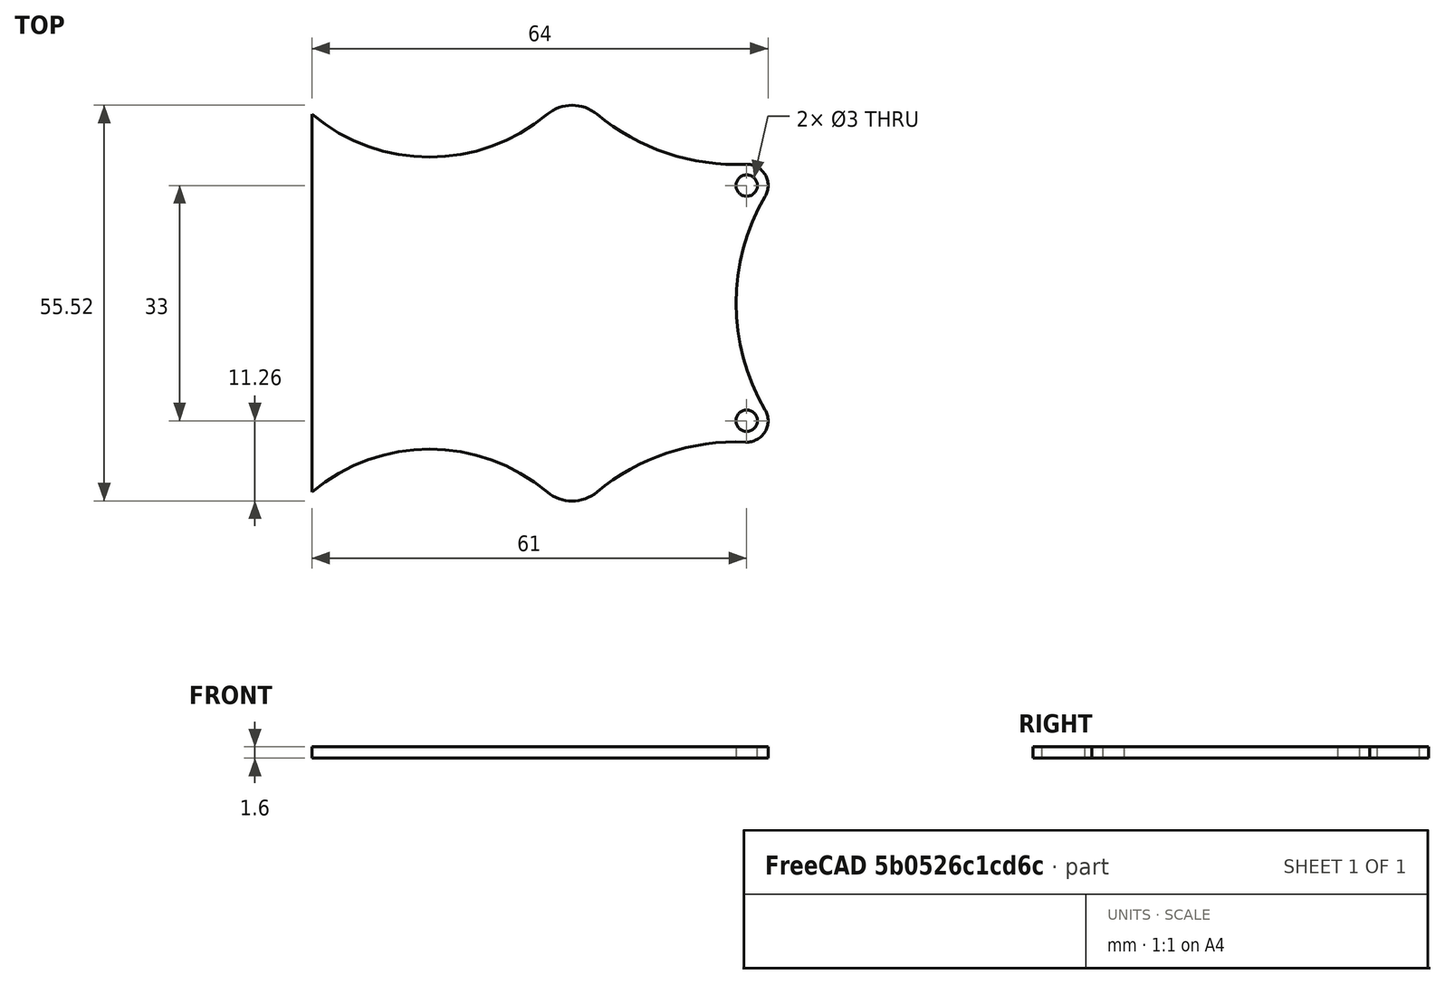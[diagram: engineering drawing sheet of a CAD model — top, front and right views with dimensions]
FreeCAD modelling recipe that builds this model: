
FCSTD DOCUMENT  (FreeCAD 0.19R24366 (Git))
Label: nixiePanelShape
License: All rights reserved
LicenseURL: http://en.wikipedia.org/wiki/All_rights_reserved
objects: Sketcher::SketchObject×1, PartDesign::Pad×1, PartDesign::Body×1
note: 4 computed .brp shape members not serialized (recipe doc carries the construction recipe); baked Part::Feature solids carry a one-line shape summary decoded from their .brp

FEATURE [Sketcher::SketchObject] Sketch
  FullyConstrained = false
  MapMode = 5
  Support = -> [XY_Plane]
  sketch-geometry (63):
    g0: LineSegment StartX=-6.5438e-12 StartY=-1.64544e-11 StartZ=0 EndX=86 EndY=-1.64544e-11 EndZ=0
    g1: LineSegment StartX=86 StartY=-1.64544e-11 StartZ=0 EndX=86 EndY=53 EndZ=0
    g2: LineSegment StartX=86 StartY=53 StartZ=0 EndX=-6.537e-12 EndY=53 EndZ=0
    g3: LineSegment StartX=-6.5438e-12 StartY=53 StartZ=0 EndX=-6.5438e-12 EndY=-1.64562e-11 EndZ=0
    g4: LineSegment StartX=3 StartY=44.5 StartZ=0 EndX=83 EndY=44.5 EndZ=0
    g5: LineSegment StartX=83 StartY=44.5 StartZ=0 EndX=83 EndY=8.5 EndZ=0
    g6: LineSegment StartX=83 StartY=8.5 StartZ=0 EndX=3 EndY=8.5 EndZ=0
    g7: LineSegment StartX=3 StartY=8.5 StartZ=0 EndX=3 EndY=44.5 EndZ=0
    g8: LineSegment StartX=3 StartY=8.5 StartZ=0 EndX=5.8074e-12 EndY=1.64544e-11 EndZ=0
    g9: LineSegment StartX=83 StartY=8.5 StartZ=0 EndX=86 EndY=-1.64544e-11 EndZ=0
    g10: LineSegment StartX=83 StartY=44.5 StartZ=0 EndX=86 EndY=53 EndZ=0
    g11: LineSegment StartX=-6.5438e-12 StartY=53 StartZ=0 EndX=3 EndY=44.5 EndZ=0
    g12: LineSegment StartX=-7 StartY=-23.5 StartZ=0 EndX=93 EndY=-23.5 EndZ=0
    g13: LineSegment StartX=93 StartY=-23.5 StartZ=0 EndX=93 EndY=76.5 EndZ=0
    g14: LineSegment StartX=93 StartY=76.5 StartZ=0 EndX=-7 EndY=76.5 EndZ=0
    g15: LineSegment StartX=-7 StartY=76.5 StartZ=0 EndX=-7 EndY=-23.5 EndZ=0
    g16: LineSegment StartX=0 StartY=0 StartZ=0 EndX=-7 EndY=-23.5 EndZ=0
    g17: LineSegment StartX=86 StartY=-1.64544e-11 StartZ=0 EndX=93 EndY=-23.5 EndZ=0
    g18: LineSegment StartX=-7 StartY=76.5 StartZ=0 EndX=-6.5441e-12 EndY=53 EndZ=0
    g19: LineSegment StartX=93 StartY=76.5 StartZ=0 EndX=86 EndY=53 EndZ=0
    g20: Circle CenterX=87.5 CenterY=43 CenterZ=0 NormalX=0 NormalY=0 NormalZ=1 AngleXU=0 Radius=1.5
    g21: Circle CenterX=87.5 CenterY=10 CenterZ=0 NormalX=0 NormalY=0 NormalZ=1 AngleXU=0 Radius=1.5
    g22: Circle CenterX=-1.5 CenterY=10 CenterZ=0 NormalX=0 NormalY=0 NormalZ=1 AngleXU=0 Radius=1.5
    g23: Circle CenterX=-1.5 CenterY=43 CenterZ=0 NormalX=0 NormalY=0 NormalZ=1 AngleXU=0 Radius=1.5
    g24: Circle CenterX=-1.5 CenterY=43 CenterZ=0 NormalX=0 NormalY=0 NormalZ=1 AngleXU=0 Radius=3
    g25: Circle CenterX=-1.5 CenterY=10 CenterZ=0 NormalX=0 NormalY=0 NormalZ=1 AngleXU=0 Radius=3
    g26: Circle CenterX=87.5 CenterY=10 CenterZ=0 NormalX=0 NormalY=0 NormalZ=1 AngleXU=0 Radius=3
    g27: Circle CenterX=87.5 CenterY=43 CenterZ=0 NormalX=0 NormalY=0 NormalZ=1 AngleXU=0 Radius=3
    g28: Circle CenterX=115.5 CenterY=26.5 CenterZ=0 NormalX=0 NormalY=0 NormalZ=1 AngleXU=0 Radius=29.5
    g29: Circle CenterX=-29.5 CenterY=26.5 CenterZ=0 NormalX=0 NormalY=0 NormalZ=1 AngleXU=0 Radius=29.5
    g30: LineSegment StartX=-1.36453e-11 StartY=63 StartZ=0 EndX=19.5 EndY=63 EndZ=0
    g31: LineSegment StartX=19.5 StartY=63 StartZ=0 EndX=26.5 EndY=63 EndZ=0
    g32: LineSegment StartX=26.5 StartY=63 StartZ=0 EndX=59.5 EndY=63 EndZ=0
    g33: LineSegment StartX=59.5 StartY=63 StartZ=0 EndX=66.5 EndY=63 EndZ=0
    g34: LineSegment StartX=66.5 StartY=63 StartZ=0 EndX=86 EndY=63 EndZ=0
    g35: LineSegment StartX=19.5 StartY=76.5 StartZ=0 EndX=19.5 EndY=-23.5 EndZ=0
    g36: LineSegment StartX=26.5 StartY=76.5 StartZ=0 EndX=26.5 EndY=-23.5 EndZ=0
    g37: LineSegment StartX=59.5 StartY=76.5 StartZ=0 EndX=59.5 EndY=-23.5 EndZ=0
    g38: LineSegment StartX=66.5 StartY=76.5 StartZ=0 EndX=66.5 EndY=-23.5 EndZ=0
    g39: Circle CenterX=1.43817e-11 CenterY=-23.5144 CenterZ=0 NormalX=0 NormalY=0 NormalZ=1 AngleXU=0 Radius=30.5479
    g40: LineSegment StartX=3 StartY=8.5 StartZ=0 EndX=19.5 EndY=-1.8062e-11 EndZ=0
    g41: Circle CenterX=86 CenterY=-23.5144 CenterZ=0 NormalX=0 NormalY=0 NormalZ=1 AngleXU=0 Radius=30.5479
    g42: Circle CenterX=0 CenterY=76.5144 CenterZ=0 NormalX=0 NormalY=0 NormalZ=1 AngleXU=0 Radius=30.5479
    g43: Circle CenterX=86 CenterY=76.5144 CenterZ=0 NormalX=0 NormalY=0 NormalZ=1 AngleXU=0 Radius=30.5479
    g44: LineSegment StartX=26.5 StartY=6 StartZ=0 EndX=59.5 EndY=6 EndZ=0
    g45: LineSegment StartX=26.5 StartY=47 StartZ=0 EndX=59.5 EndY=47 EndZ=0
    g46: LineSegment StartX=26.5 StartY=53 StartZ=0 EndX=43 EndY=47 EndZ=0
    g47: LineSegment StartX=43 StartY=47 StartZ=0 EndX=59.5 EndY=53 EndZ=0
    g48: LineSegment StartX=26.5 StartY=-1.64562e-11 StartZ=0 EndX=43 EndY=6 EndZ=0
    g49: LineSegment StartX=43 StartY=6 StartZ=0 EndX=59.5 EndY=-1.64562e-11 EndZ=0
    g50: Circle CenterX=43 CenterY=-19.6875 CenterZ=0 NormalX=0 NormalY=0 NormalZ=1 AngleXU=0 Radius=25.6875
    g51: Circle CenterX=43 CenterY=72.6875 CenterZ=0 NormalX=0 NormalY=0 NormalZ=1 AngleXU=0 Radius=25.6875
    g52: ArcOfCircle CenterX=23 CenterY=4.22058 CenterZ=0 NormalX=0 NormalY=0 NormalZ=1 AngleXU=0 Radius=5.483 StartAngle=4.02005 EndAngle=5.40472
    g53: ArcOfCircle CenterX=43 CenterY=-19.6875 CenterZ=0 NormalX=0 NormalY=0 NormalZ=1 AngleXU=0 Radius=25.6875 StartAngle=0.873254 EndAngle=2.26834
    g54: ArcOfCircle CenterX=63 CenterY=4.22049 CenterZ=0 NormalX=0 NormalY=0 NormalZ=1 AngleXU=0 Radius=5.48293 StartAngle=4.02004 EndAngle=5.40474
    g55: ArcOfCircle CenterX=86 CenterY=-23.5144 CenterZ=0 NormalX=0 NormalY=0 NormalZ=1 AngleXU=0 Radius=30.5479 StartAngle=1.52607 EndAngle=2.26314
    g56: ArcOfCircle CenterX=115.5 CenterY=26.5 CenterZ=0 NormalX=0 NormalY=0 NormalZ=1 AngleXU=0 Radius=29.5 StartAngle=2.60909 EndAngle=3.6741
    g57: ArcOfCircle CenterX=87.5 CenterY=10 CenterZ=0 NormalX=0 NormalY=0 NormalZ=1 AngleXU=0 Radius=3 StartAngle=4.66766 EndAngle=6.81569
    g58: ArcOfCircle CenterX=86 CenterY=76.5144 CenterZ=0 NormalX=0 NormalY=0 NormalZ=1 AngleXU=0 Radius=30.5479 StartAngle=4.02005 EndAngle=4.75712
    g59: ArcOfCircle CenterX=87.5 CenterY=43 CenterZ=0 NormalX=0 NormalY=0 NormalZ=1 AngleXU=0 Radius=3.00002 StartAngle=5.75069 EndAngle=7.8987
    g60: ArcOfCircle CenterX=43 CenterY=72.6875 CenterZ=0 NormalX=0 NormalY=0 NormalZ=1 AngleXU=0 Radius=25.6875 StartAngle=4.01485 EndAngle=5.40993
    g61: ArcOfCircle CenterX=63 CenterY=48.7794 CenterZ=0 NormalX=0 NormalY=0 NormalZ=1 AngleXU=0 Radius=5.48303 StartAngle=0.878466 EndAngle=2.26313
    g62: LineSegment StartX=26.5 StartY=-1.64562e-11 StartZ=0 EndX=26.5 EndY=53 EndZ=0
  constraints (189):
    c: Coincident(g0,g1)
    c: Coincident(g1,g2)
    c: Coincident(g2,g3)
    c: Coincident(g3,g0)
    c: Horizontal(g0)
    c: Horizontal(g2)
    c: Vertical(g1)
    c: Vertical(g3)
    c: Coincident(g0,g-1)
    c: Coincident(g4,g5)
    c: Coincident(g5,g6)
    c: Coincident(g6,g7)
    c: Coincident(g7,g4)
    c: Horizontal(g4)
    c: Horizontal(g6)
    c: Vertical(g5)
    c: Vertical(g7)
    c: Distance(g4) = 80
    c: Distance(g7) = 36
    c: Distance(g3) = 53
    c: Distance(g2) = 86
    c: Coincident(g8,g6)
    c: Coincident(g8,g-1)
    c: Coincident(g9,g5)
    c: Coincident(g10,g4)
    c: Coincident(g10,g1)
    c: Coincident(g11,g2)
    c: Coincident(g11,g4)
    c: Coincident(g9,g0)
    c: Equal(g11,g8)
    c: Equal(g8,g9)
    c: Coincident(g12,g13)
    c: Coincident(g13,g14)
    c: Coincident(g14,g15)
    c: Coincident(g15,g12)
    c: Horizontal(g12)
    c: Horizontal(g14)
    c: Vertical(g13)
    c: Vertical(g15)
    c: Equal(g14,g15)
    c: Distance(g15) = 100
    c: Coincident(g16,g-1)
    c: Coincident(g16,g12)
    c: Coincident(g17,g0)
    c: Coincident(g17,g12)
    c: Coincident(g18,g14)
    c: Coincident(g18,g2)
    c: Coincident(g19,g13)
    c: Coincident(g19,g1)
    c: Equal(g17,g16)
    c: Equal(g16,g18)
    c: Equal(g22,g23)
    c: Equal(g23,g20)
    c: Equal(g20,g21)
    c: Radius(g20) = 1.5
    c: Tangent(g22,g3)
    c: Tangent(g23,g3)
    c: Tangent(g20,g1)
    c: Tangent(g21,g1)
    c: Coincident(g24,g23)
    c: Coincident(g25,g22)
    c: Coincident(g26,g21)
    c: Coincident(g27,g20)
    c: Equal(g24,g25)
    c: Equal(g25,g26)
    c: Equal(g26,g27)
    c: Radius(g24) = 3
    c: Tangent(g28,g27)
    c: Tangent(g28,g26)
    c: Tangent(g28,g1)
    c: Tangent(g29,g24)
    c: Tangent(g29,g25)
    c: Tangent(g29,g3)
    c: PointOnObject(g30,g-2)
    c: Horizontal(g30)
    c: Coincident(g30,g31)
    c: Horizontal(g31)
    c: Coincident(g31,g32)
    c: Horizontal(g32)
    c: Coincident(g32,g33)
    c: Horizontal(g33)
    c: Coincident(g33,g34)
    c: Horizontal(g34)
    c: Equal(g30,g34)
    c: Equal(g31,g33)
    c: Distance(g32) = 33
    c: Distance(g30) = 19.5
    c: Distance(g30,g2) = 10
    c: PointOnObject(g35,g14)
    c: PointOnObject(g35,g12)
    c: Vertical(g35)
    c: PointOnObject(g36,g14)
    c: PointOnObject(g36,g12)
    c: Vertical(g36)
    c: PointOnObject(g37,g14)
    c: PointOnObject(g37,g12)
    c: Vertical(g37)
    c: PointOnObject(g38,g14)
    c: PointOnObject(g38,g12)
    c: Vertical(g38)
    c: PointOnObject(g30,g35)
    c: PointOnObject(g31,g36)
    c: PointOnObject(g32,g37)
    c: PointOnObject(g33,g38)
    c: PointOnObject(g39,g-2)
    c: Tangent(g39,g25)
    c: Coincident(g40,g6)
    c: PointOnObject(g40,g0)
    c: PointOnObject(g40,g35)
    c: PointOnObject(g40,g39)
    c: Tangent(g26,g41)
    c: PointOnObject(g41,g1)
    c: Equal(g39,g41)
    c: PointOnObject(g34,g1)
    c: PointOnObject(g42,g-2)
    c: PointOnObject(g43,g1)
    c: Tangent(g43,g27)
    c: Tangent(g42,g24)
    c: Equal(g42,g43)
    c: Equal(g43,g39)
    c: PointOnObject(g44,g36)
    c: PointOnObject(g44,g37)
    c: Horizontal(g44)
    c: PointOnObject(g45,g36)
    c: PointOnObject(g45,g37)
    c: Horizontal(g45)
    c: Distance(g45,g4) = 2.5
    c: Distance(g44,g6) = 2.5
    c: PointOnObject(g46,g2)
    c: PointOnObject(g46,g45)
    c: PointOnObject(g47,g2)
    c: PointOnObject(g46,g36)
    c: PointOnObject(g47,g37)
    c: Equal(g47,g46)
    c: Coincident(g46,g47)
    c: PointOnObject(g48,g0)
    c: PointOnObject(g48,g44)
    c: Coincident(g48,g49)
    c: PointOnObject(g49,g0)
    c: PointOnObject(g48,g36)
    c: PointOnObject(g49,g37)
    c: Equal(g49,g48)
    c: PointOnObject(g48,g50)
    c: PointOnObject(g48,g50)
    c: PointOnObject(g49,g50)
    c: PointOnObject(g46,g51)
    c: PointOnObject(g47,g51)
    c: PointOnObject(g46,g51)
    c: Coincident(g52,g40)
    c: Coincident(g52,g48)
    c: Tangent(g52,g39)
    c: Coincident(g53,g52)
    c: Coincident(g53,g49)
    c: PointOnObject(g48,g53)
    c: Coincident(g54,g53)
    c: PointOnObject(g54,g41)
    c: PointOnObject(g54,g38)
    c: Tangent(g54,g41)
    c: Coincident(g55,g54)
    c: PointOnObject(g55,g26)
    c: PointOnObject(g55,g41)
    c: PointOnObject(g56,g26)
    c: Tangent(g56,g26)
    c: PointOnObject(g56,g27)
    c: PointOnObject(g56,g28)
    c: Coincident(g57,g55)
    c: Coincident(g56,g57)
    c: Tangent(g57,g28)
    c: PointOnObject(g58,g38)
    c: PointOnObject(g58,g2)
    c: PointOnObject(g58,g27)
    c: PointOnObject(g58,g43)
    c: Coincident(g56,g59)
    c: Coincident(g59,g58)
    c: Tangent(g59,g43)
    c: Coincident(g61,g58)
    c: Coincident(g61,g47)
    c: Coincident(g60,g61)
    c: Coincident(g60,g46)
    c: Coincident(g62,g53)
    c: Coincident(g62,g60)
    c: PointOnObject(g46,g60)
    c: Tangent(g6,g21)
    c: Tangent(g4,g20)
    c: Tangent(g23,g4)
    c: Tangent(g22,g6)
    c: Tangent(g58,g43)
    c: Tangent(g56,g28)
    c: Tangent(g61,g43)
FEATURE [PartDesign::Pad] Pad
  Direction = (1,1,1)
  Length = 1.6
  Length2 = 100
  Profile = -> Sketch
  Refine = true
  Type = 0
FEATURE [PartDesign::Body] Body
  Group = -> [Sketch,Pad]
  Origin = -> Origin
  Tip = -> Pad
